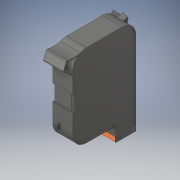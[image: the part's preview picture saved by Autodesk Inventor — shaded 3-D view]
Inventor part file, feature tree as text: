
AUTODESK INVENTOR PART (.ipt)
format: ipt  version: 2018 (Build 220112000, 112)  size: 412,672 bytes
history: native  units: in
note: dims shown in document units (in); Inventor stores cm internally (conversion verified against a paired STEP export)
features: other x1, mirror x1
ambient origin geometry x8: Origin, YZ Plane, XZ Plane, XY Plane, X Axis, Y Axis, Z Axis, Center Point
bodies: Solid1 (feature_tree), Solid2 (feature_tree)
feature tree (2):
  other  "Cut-Extrude5"
  mirror  "Mirror3"
